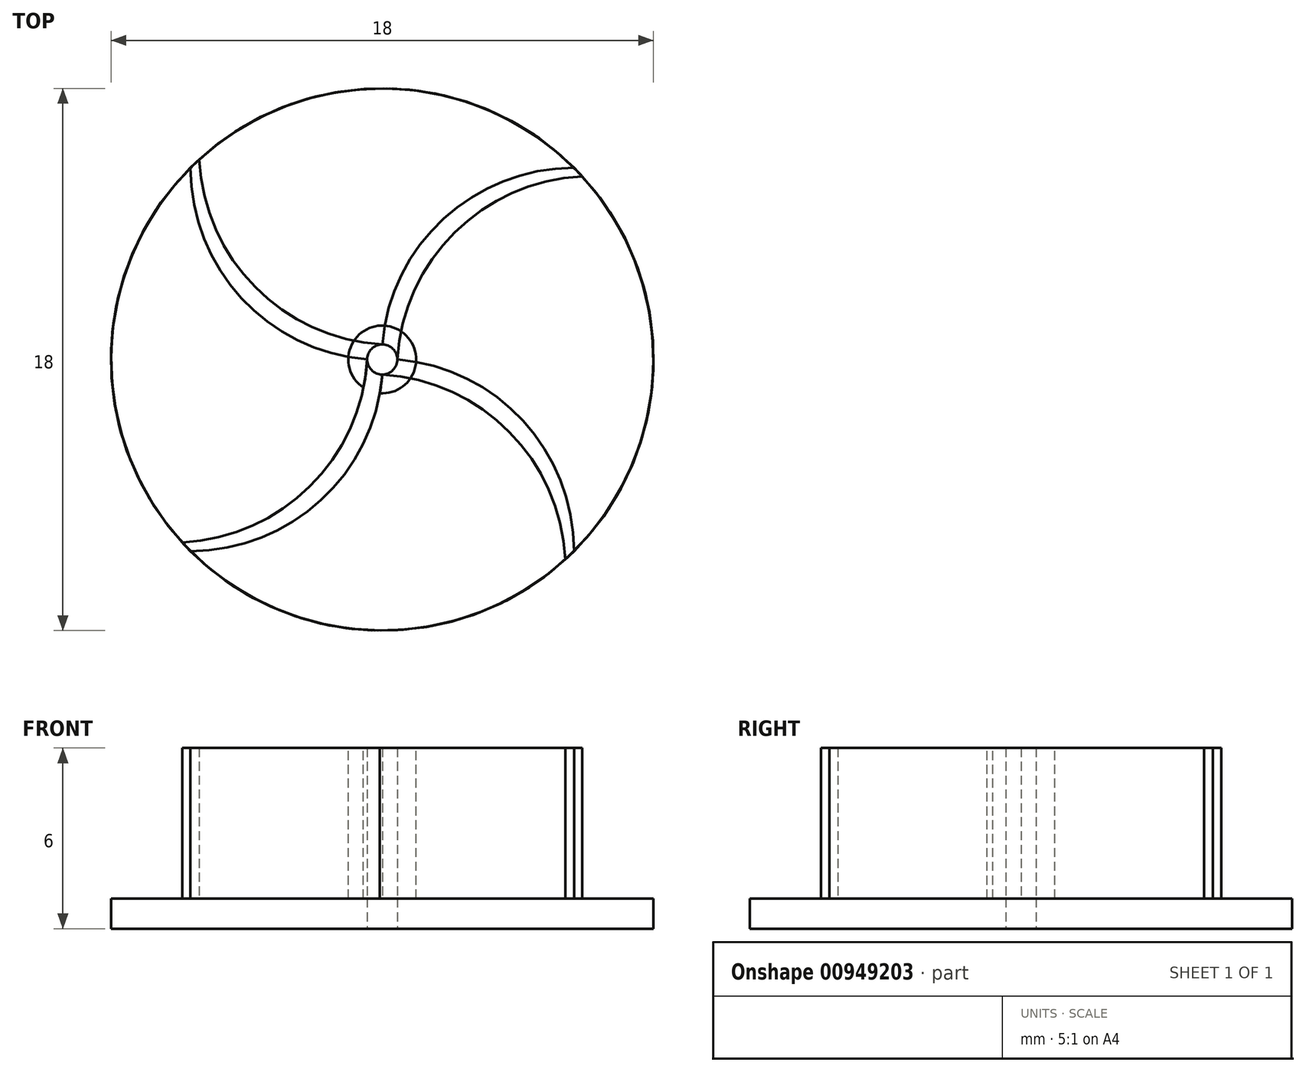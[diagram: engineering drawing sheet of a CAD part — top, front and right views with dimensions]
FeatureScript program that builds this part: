
annotation { "Feature Type Name" : "Feature", "Feature Type Description" : "" }
export const myFeature = defineFeature(function(context is Context, id is Id, definition is map)
    precondition{}
    {
        {
            var Q0;
            Q0=qCreatedBy(makeId("Top.planeOp"),FACE);
            var sketch = newSketch(context, id + "F0", { "sketchPlane" : qUnion([Q0])});
            skCircle(sketch, "E0", {"center": v(0, 0) * mm, "radius": 9 * mm});
            skCircle(sketch, "E1", {"center": v(0, 0) * mm, "radius": 0.5 * mm});
            skSolve(sketch);
        }
        {
            var Q0;
            Q0=makeQuery(id+"F0.imprint","IMPRINT",FACE,{"disambiguationData":[TD([[makeQuery(id+"F0.imprint","IMPRINT",EDGE,{"derivedFrom":sQuery(id+"F0.wireOp",EDGE,"E0")}),1.0]])]});
            extrude(context, id + "F1", {"entities" : qUnion([Q0]), "depth" : 1 * mm, "offsetDistance" : 25 * mm});
        }
        {
            var Q0;
            Q0=makeQuery(id+"F1.opExtrude","CAP_FACE",FACE,{"disambiguationData":[OSD([sQuery(id+"F0.wireOp",EDGE,"E0"),sQuery(id+"F0.wireOp",EDGE,"E1")])],"isStart":false});
            var sketch = newSketch(context, id + "F2", { "sketchPlane" : qUnion([Q0])});
            skPoint(sketch, "E2.middle", {"position": v(0, 0) * mm});
            skArc(sketch, "E3", {"start": v(6.36, 6.36) * mm, "mid": v(2.04, 4.67) * mm, "end": v(0, 0.5) * mm});
            skArc(sketch, "E4", {"start": v(6.64, 6.08) * mm, "mid": v(2.4, 4.22) * mm, "end": v(0.5, 0) * mm});
            skPoint(sketch, "E2.left.start.orphan", {"position": v(-6.36, 6.36) * mm});
            skPoint(sketch, "E2.top.end.orphan", {"position": v(6.36, -6.36) * mm});
            skPoint(sketch, "E2.top.start.orphan", {"position": v(-6.36, -6.36) * mm});
            skLineSegment(sketch, "E5", {"start": v(6.36, 6.36) * mm, "end": v(6.64, 6.08) * mm});
            skArc(sketch, "E6", {"start": v(0.5, 0) * mm, "mid": v(0.35, 0.35) * mm, "end": v(0, 0.5) * mm});
            skSolve(sketch);
        }
        {
            var Q0;
            Q0=makeQuery(id+"F2.imprint","IMPRINT",FACE,{"disambiguationData":[TD([[makeQuery(id+"F2.imprint","IMPRINT",EDGE,{"derivedFrom":sQuery(id+"F2.wireOp",EDGE,"E3")}),1.0]])]});
            extrude(context, id + "F3", {"entities" : qUnion([Q0]), "operationType" : NewBodyOperationType.ADD, "depth" : 5 * mm, "offsetDistance" : 25 * mm});
        }
        {
            var Q0;
            Q0=makeQuery(id+"F1.opExtrude","SWEPT_BODY",BODY,{"disambiguationData":[OSD([sQuery(id+"F0.wireOp",EDGE,"E0"),sQuery(id+"F0.wireOp",EDGE,"E1")])]});
            var Q1;
            Q1=makeQuery(id+"F1.opExtrude","CAP_EDGE",EDGE,{"disambiguationData":[OSD([sQuery(id+"F0.wireOp",EDGE,"E1")])],"isStart":false});
            circularPattern(context, id + "F4", {"entities" : qUnion([Q0]), "axis" : qUnion([Q1]), "angle" : 360 * degree, "instanceCount" : 4, "equalSpace" : true});
        }
        {
            var Q0;
            Q0=makeQuery(id+"F4.opPattern","COPY",FACE,{"derivedFrom":makeQuery(id+"F3.opExtrude","CAP_FACE",FACE,{"disambiguationData":[OSD([sQuery(id+"F2.wireOp",EDGE,"E3"),sQuery(id+"F2.wireOp",EDGE,"E4"),sQuery(id+"F2.wireOp",EDGE,"E5"),sQuery(id+"F2.wireOp",EDGE,"E6")])],"isStart":false}),"instanceName":"2"});
            var sketch = newSketch(context, id + "F5", { "sketchPlane" : qUnion([Q0])});
            skCircle(sketch, "E7", {"center": v(0, 0) * mm, "radius": 0.5 * mm});
            skCircle(sketch, "E8", {"center": v(0, 0) * mm, "radius": 1.13 * mm});
            skSolve(sketch);
        }
        {
            var Q0;
            {var subQ0=sQuery(id+"F5.wireOp",EDGE,"E7");var subQ1=makeQuery(id+"F4.opPattern","COPY",EDGE,{"derivedFrom":makeQuery(id+"F3.opExtrude","CAP_EDGE",EDGE,{"disambiguationData":[OSD([sQuery(id+"F2.wireOp",EDGE,"E3")])],"isStart":false}),"instanceName":"2"});var subQ2=makeQuery(id+"F5.imprint","INTERSECT",VERTEX,{"derivedFrom":[subQ1,subQ0]});Q0=makeQuery(id+"F5.imprint","IMPRINT",FACE,{"disambiguationData":[TD([[makeQuery(id+"F5.imprint","IMPRINT",EDGE,{"disambiguationData":[TD([[subQ2,-1.0]])],"derivedFrom":subQ0}),-1.0]])]});}
            extrude(context, id + "F6", {"entities" : qUnion([Q0]), "oppositeDirection" : true, "depth" : 5 * mm, "offsetDistance" : 25 * mm});
        }
    });
